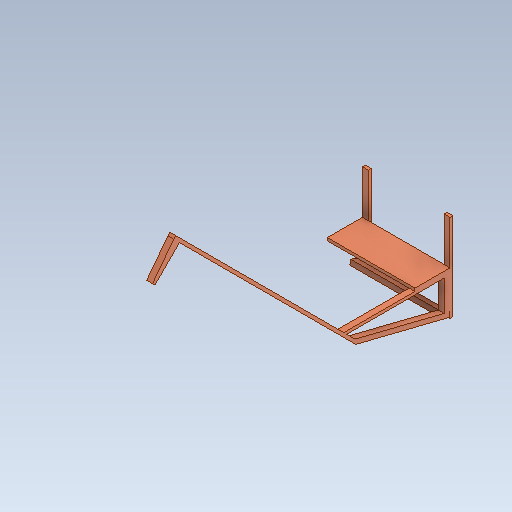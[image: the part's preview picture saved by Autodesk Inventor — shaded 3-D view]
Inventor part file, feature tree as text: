
AUTODESK INVENTOR PART (.ipt)
format: ipt  version: 2021.1 (Build 251245000, 245)  size: 146,432 bytes
history: native  units: in
note: dims shown in document units (in); Inventor stores cm internally (conversion verified against a paired STEP export)
features: sketch x6, other x3, plane x1
ambient origin geometry x8: Origin, YZ Plane, XZ Plane, XY Plane, X Axis, Y Axis, Z Axis, Center Point
bodies: Solid1 (feature_tree)
feature tree (10):
  other  "side1.ipt"
  other  "Solid2::side1.ipt"
  other  "TaggingFeature1"
  sketch  "Sketch1"  dims[d0=0.3937in]
  sketch  "Sketch2"
  sketch  "Sketch3"
  sketch  "Sketch4"
  sketch  "Sketch5"
  sketch  "Sketch7"
  plane  "Work Plane1"
